# Revit family: Модуль с мойкой односекционной и дверцей ДМ
name_source: partatom
category: Оборудование
revit_build: Autodesk Revit 2017 (Build: 20170118_1100(x64)
units: mm (PartAtom-declared; Revit-internal decimal feet)

## family parameters
Всегда вертикально = Да
На основе рабочей плоскости = Нет
Общий = Нет
При загрузке вырезать с полостями = Нет
Размер круглого соединителя = Использовать диаметр
Тип детали = Нормальный
Точка расчета площади = Нет

## types (1)
- Тип
    Каркас = Алюминий 7075
    Мойка = Сталь, нержавеющая AISI 304
    Ножки = Пластмасса, непрозрачная, черная
    Общ_Высота = 820 мм
    Общ_Глубина = 600 мм
    Общ_Диаметр ГВ = 13 мм
    Общ_Диаметр К = 50.00 мм
    Общ_Диаметр ХВ = 13 мм
    Общ_Единицы измерения = шт.
    Общ_Наименование = Стол медицинский однотумбовый из ЛДСП на алюминиевом каркасе, с тремя выдвижными ящиками
    Общ_Поставщик = Доктор Мебель
    Общ_Тип, марка = ДМ-2-006-15
    Общ_Ширина = 1200 мм
    Панели = Пластмасса, непрозрачная, белая
    Фасад = Столешница медицинской мебели ДСП с пластиковым покрытием
